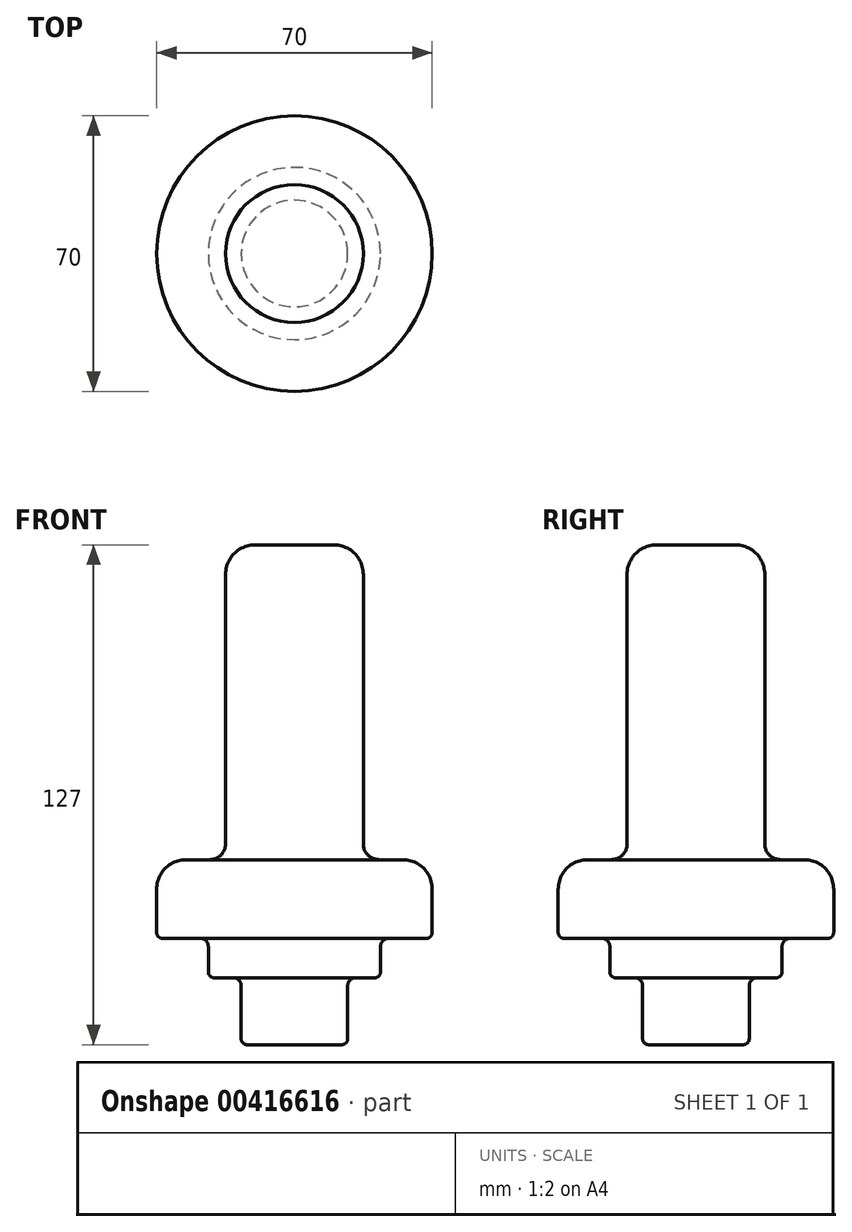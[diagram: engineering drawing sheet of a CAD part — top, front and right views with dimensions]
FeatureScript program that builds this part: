
annotation { "Feature Type Name" : "Feature", "Feature Type Description" : "" }
export const myFeature = defineFeature(function(context is Context, id is Id, definition is map)
    precondition{}
    {
        {
            var Q0;
            Q0=qCreatedBy(makeId("Front.planeOp"),FACE);
            var sketch = newSketch(context, id + "F0", { "sketchPlane" : qUnion([Q0])});
            skLineSegment(sketch, "E0.bottom", {"start": v(0, 0) * mm, "end": v(-12.04, 0) * mm});
            skLineSegment(sketch, "E0.top", {"start": v(0, 17) * mm, "end": v(-14.54, 17) * mm});
            skLineSegment(sketch, "E0.left", {"start": v(0, 0) * mm, "end": v(0, 17) * mm});
            skLineSegment(sketch, "E0.right", {"start": v(-13.54, 1.5) * mm, "end": v(-13.54, 15) * mm});
            skLineSegment(sketch, "E1.bottom", {"start": v(-15.54, 17) * mm, "end": v(-20.38, 17) * mm});
            skLineSegment(sketch, "E1.top", {"start": v(0, 27) * mm, "end": v(-22.38, 27) * mm});
            skLineSegment(sketch, "E1.left", {"start": v(0, 17) * mm, "end": v(0, 27) * mm});
            skLineSegment(sketch, "E1.right", {"start": v(-21.88, 18.5) * mm, "end": v(-21.88, 25) * mm});
            skLineSegment(sketch, "E2.bottom", {"start": v(-23.88, 27) * mm, "end": v(-33.5, 27) * mm});
            skLineSegment(sketch, "E2.top", {"start": v(-21.5, 47) * mm, "end": v(-27.5, 47) * mm});
            skLineSegment(sketch, "E2.left", {"start": v(0, 27) * mm, "end": v(0, 47) * mm});
            skLineSegment(sketch, "E2.right", {"start": v(-35, 28.5) * mm, "end": v(-35, 39.5) * mm});
            skPoint(sketch, "E3.oppositeSnap0", {"position": v(-17.5, 47) * mm});
            skLineSegment(sketch, "E3.top", {"start": v(0, 127) * mm, "end": v(-10, 127) * mm});
            skLineSegment(sketch, "E3.left", {"start": v(0, 47) * mm, "end": v(0, 127) * mm});
            skLineSegment(sketch, "E3.right", {"start": v(-17.5, 51) * mm, "end": v(-17.5, 119.5) * mm});
            skPoint(sketch, "E4.visualSharp", {"position": v(-17.5, 127) * mm});
            skArc(sketch, "E4.filletArc", {"start": v(-10, 127) * mm, "mid": v(-15.3, 124.8) * mm, "end": v(-17.5, 119.5) * mm});
            skPoint(sketch, "E5.visualSharp", {"position": v(-35, 47) * mm});
            skArc(sketch, "E5.filletArc", {"start": v(-27.5, 47) * mm, "mid": v(-32.8, 44.8) * mm, "end": v(-35, 39.5) * mm});
            skPoint(sketch, "E6.visualSharp", {"position": v(-35, 27) * mm});
            skArc(sketch, "E6.filletArc", {"start": v(-35, 28.5) * mm, "mid": v(-34.56, 27.44) * mm, "end": v(-33.5, 27) * mm});
            skPoint(sketch, "E7.visualSharp", {"position": v(-21.88, 17) * mm});
            skArc(sketch, "E7.filletArc", {"start": v(-21.88, 18.5) * mm, "mid": v(-21.44, 17.44) * mm, "end": v(-20.38, 17) * mm});
            skPoint(sketch, "E8.visualSharp", {"position": v(-13.54, 0) * mm});
            skArc(sketch, "E8.filletArc", {"start": v(-13.54, 1.5) * mm, "mid": v(-13.1, 0.44) * mm, "end": v(-12.04, 0) * mm});
            skPoint(sketch, "E9.newPointB", {"position": v(-13.54, 17) * mm});
            skArc(sketch, "E9.filletArc", {"start": v(-13.54, 15) * mm, "mid": v(-14.13, 16.41) * mm, "end": v(-15.54, 17) * mm});
            skArc(sketch, "E10.filletArc", {"start": v(-21.88, 25) * mm, "mid": v(-22.47, 26.41) * mm, "end": v(-23.88, 27) * mm});
            skPoint(sketch, "E11.newPointB", {"position": v(0, 47) * mm});
            skArc(sketch, "E11.filletArc", {"start": v(-21.5, 47) * mm, "mid": v(-18.67, 48.17) * mm, "end": v(-17.5, 51) * mm});
            skLineSegment(sketch, "E12", {"start": v(0, -28.36) * mm, "end": v(0, 131.29) * mm});
            skSolve(sketch);
        }
        {
            var Q0;
            {var subQ1=sQuery(id+"F0.wireOp",EDGE,"E0.bottom");Q0=makeQuery(id+"F0.imprint","IMPRINT",FACE,{"disambiguationData":[TD([[makeQuery(id+"F0.imprint","IMPRINT",EDGE,{"derivedFrom":subQ1}),-1.0]])]});}
            var Q1;
            Q1=qConstructionFilter(qBodyType(qCreatedBy(id+"F0",EDGE),BodyType.WIRE),ConstructionObject.NO);
            var Q2;
            Q2=sQuery(id+"F0.wireOp",EDGE,"E12");
            revolve(context, id + "F1", {"entities" : qUnion([Q0]), "surfaceEntities" : qUnion([Q1]), "axis" : qUnion([Q2]), "revolveType" : RevolveType.FULL});
        }
    });
